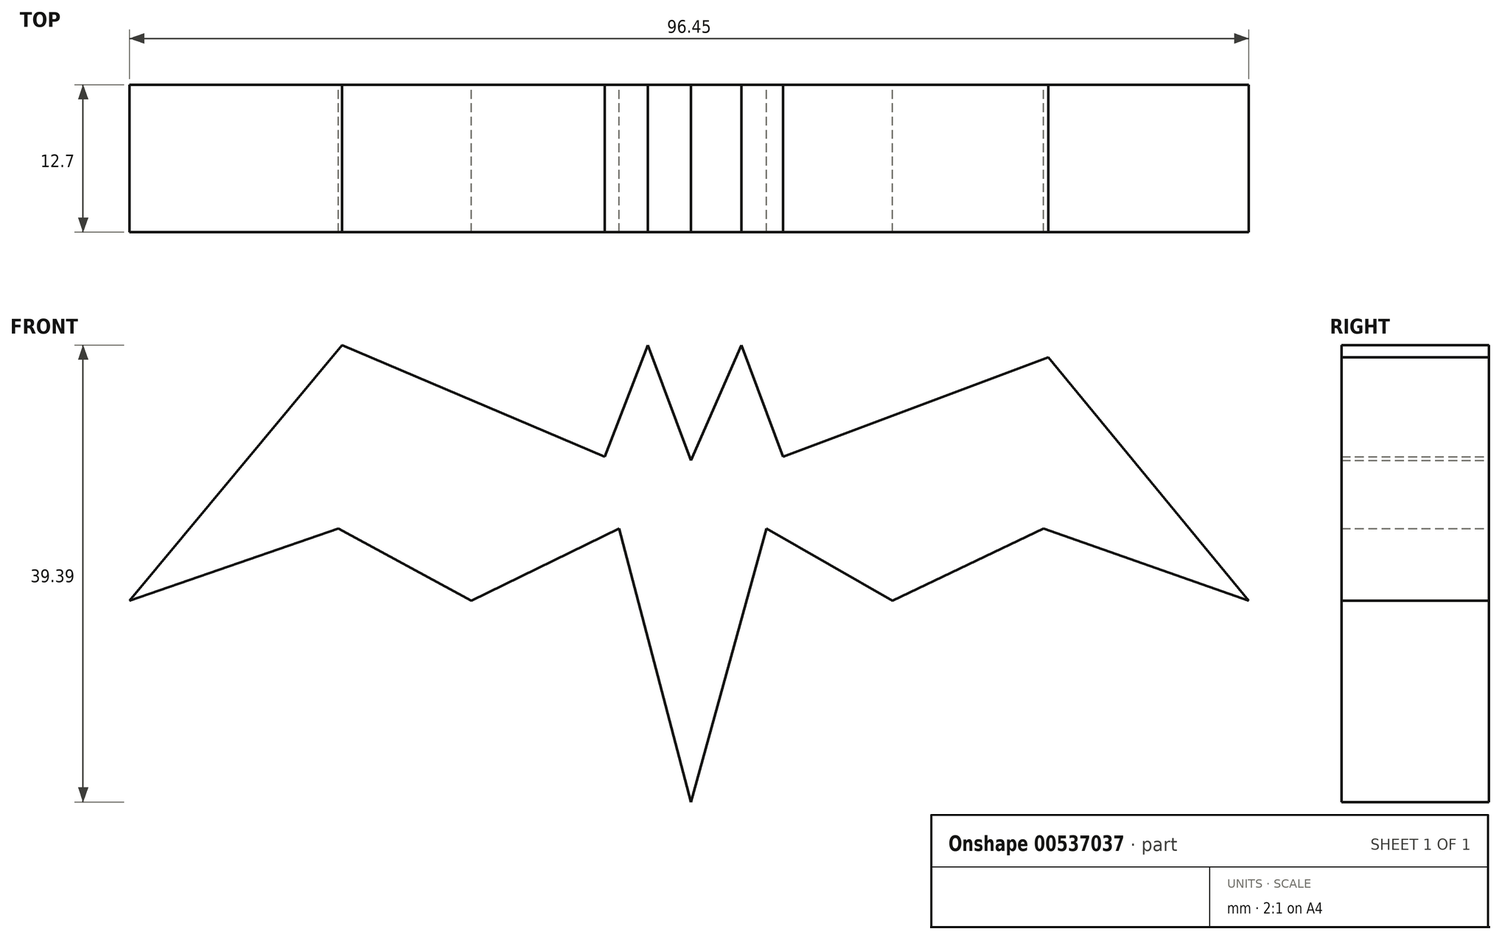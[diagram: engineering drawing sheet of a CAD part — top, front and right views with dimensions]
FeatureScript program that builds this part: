
annotation { "Feature Type Name" : "Feature", "Feature Type Description" : "" }
export const myFeature = defineFeature(function(context is Context, id is Id, definition is map)
    precondition{}
    {
        {
            var Q0;
            Q0=qCreatedBy(makeId("Front.planeOp"),FACE);
            var sketch = newSketch(context, id + "F0", { "sketchPlane" : qUnion([Q0])});
            skLineSegment(sketch, "E0", {"start": v(0, 12.1) * mm, "end": v(-3.72, 22.02) * mm});
            skLineSegment(sketch, "E1", {"start": v(-3.72, 22.02) * mm, "end": v(-7.44, 12.4) * mm});
            skLineSegment(sketch, "E2", {"start": v(0, 12.1) * mm, "end": v(4.34, 22.02) * mm});
            skLineSegment(sketch, "E3", {"start": v(4.34, 22.02) * mm, "end": v(7.95, 12.4) * mm});
            skLineSegment(sketch, "E4", {"start": v(-7.44, 12.4) * mm, "end": v(-30.08, 22.02) * mm});
            skLineSegment(sketch, "E5", {"start": v(-30.08, 22.02) * mm, "end": v(-48.38, 0) * mm});
            skLineSegment(sketch, "E6", {"start": v(7.95, 12.4) * mm, "end": v(30.78, 20.97) * mm});
            skLineSegment(sketch, "E7", {"start": v(30.78, 20.97) * mm, "end": v(48.07, 0) * mm});
            skLineSegment(sketch, "E8", {"start": v(48.07, 0) * mm, "end": v(30.4, 6.2) * mm});
            skLineSegment(sketch, "E9", {"start": v(-48.38, 0) * mm, "end": v(-30.4, 6.2) * mm});
            skLineSegment(sketch, "E10", {"start": v(-30.4, 6.2) * mm, "end": v(-18.92, 0) * mm});
            skLineSegment(sketch, "E11", {"start": v(30.4, 6.2) * mm, "end": v(17.37, 0) * mm});
            skLineSegment(sketch, "E12", {"start": v(17.37, 0) * mm, "end": v(6.51, 6.2) * mm});
            skLineSegment(sketch, "E13", {"start": v(-18.92, 0) * mm, "end": v(-6.2, 6.2) * mm});
            skLineSegment(sketch, "E14", {"start": v(-6.2, 6.2) * mm, "end": v(0, -17.37) * mm});
            skLineSegment(sketch, "E15", {"start": v(0, -17.37) * mm, "end": v(6.51, 6.2) * mm});
            skSolve(sketch);
        }
        {
            var Q0;
            Q0 = qSketchRegion(id + "F0", true);
            extrude(context, id + "F1", {"entities" : qUnion([Q0]), "depth" : 12.7 * mm, "offsetDistance" : 25.4 * mm});
        }
    });
